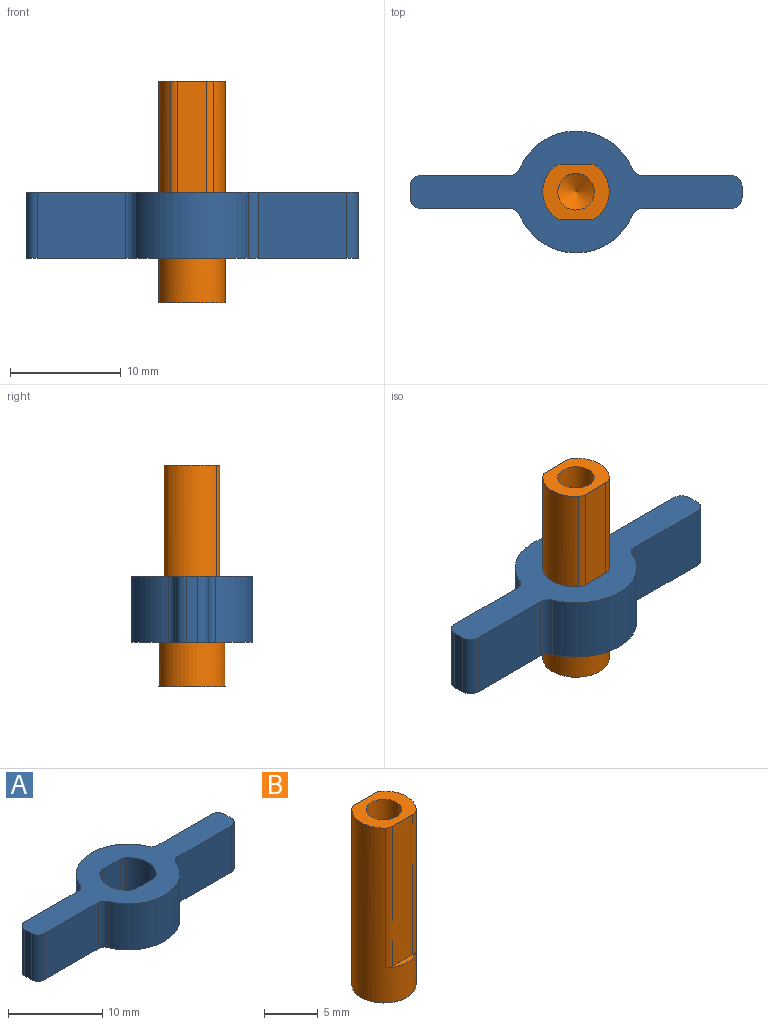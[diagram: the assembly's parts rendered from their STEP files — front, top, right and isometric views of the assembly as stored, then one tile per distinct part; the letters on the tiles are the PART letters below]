
ASSEMBLY  parts=2 mates=1
PART A: 26 faces, bbox 30x11x6 mm
  f0: plane 8x6mm, normal (0,-1,0), area 48mm2, adj f12,f13,f15,f19
  f1: cylinder r=5.5mm len=10.15mm, axis (0,0,-1), area 77.6mm2, adj f12,f13,f19,f20
  f2: plane 8x6mm, normal (0,-1,0), area 48mm2, adj f12,f13,f16,f20
  f3: plane 6x1mm, normal (1,0,0), area 6mm2, adj f12,f13,f16,f17
  f4: plane 8x6mm, normal (0,1,0), area 48mm2, adj f12,f13,f17,f23
  f5: cylinder r=5.5mm len=10.15mm, axis (0,0,-1), area 77.6mm2, adj f12,f13,f22,f23
  f6: plane 8x6mm, normal (0,1,0), area 48mm2, adj f12,f13,f14,f22
  f7: cylinder r=3mm len=6mm, axis (0,0,-1), area 30.5mm2, adj f12,f13,f18,f24
  f8: plane 6x2.65mm, normal (0,-1,0), area 15.9mm2, adj f12,f13,f24,f25
  f9: cylinder r=3mm len=6mm, axis (0,0,-1), area 30.5mm2, adj f12,f13,f21,f25
  f10: plane 6x2.65mm, normal (0,1,0), area 15.9mm2, adj f12,f13,f18,f21
  f11: plane 6x1mm, normal (-1,0,0), area 6mm2, adj f12,f13,f14,f15
  f12: plane 30x11mm, normal (0,0,1), area 126mm2, adj f0,f1,f2,f3,f4,f5,f6,f7
  f13: plane 30x11mm, normal (0,0,-1), area 126mm2, adj f0,f1,f2,f3,f4,f5,f6,f7
  f14: cylinder r=1mm len=6mm, axis (0,0,1), area 9.4mm2, adj f6,f11,f12,f13
  f15: cylinder r=1mm len=6mm, axis (0,0,-1), area 9.4mm2, adj f0,f11,f12,f13
  f16: cylinder r=1mm len=6mm, axis (0,0,1), area 9.4mm2, adj f2,f3,f12,f13
  f17: cylinder r=1mm len=6mm, axis (0,0,-1), area 9.4mm2, adj f3,f4,f12,f13
  f18: cylinder r=1mm len=6mm, axis (0,0,-1), area 4.3mm2, adj f7,f10,f12,f13
  f19: cylinder r=1mm len=6mm, axis (0,0,-1), area 7.1mm2, adj f0,f1,f12,f13
  f20: cylinder r=1mm len=6mm, axis (0,0,-1), area 7.1mm2, adj f1,f2,f12,f13
  f21: cylinder r=1mm len=6mm, axis (0,0,-1), area 4.3mm2, adj f9,f10,f12,f13
  f22: cylinder r=1mm len=6mm, axis (0,0,-1), area 7.1mm2, adj f5,f6,f12,f13
  f23: cylinder r=1mm len=6mm, axis (0,0,-1), area 7.1mm2, adj f4,f5,f12,f13
  f24: cylinder r=1mm len=6mm, axis (0,0,-1), area 4.3mm2, adj f7,f8,f12,f13
  f25: cylinder r=1mm len=6mm, axis (0,0,-1), area 4.3mm2, adj f8,f9,f12,f13
PART B: 13 faces, bbox 6x6x20 mm
  f0: plane 6x5mm, normal (0,0,1), area 17.4mm2, adj f1,f3,f5,f7,f9,f10,f11,f12
  f1: cylinder r=3mm len=20mm, axis (0,0,-1), area 238.2mm2, adj f0,f2,f4,f6,f9,f10,f11,f12
  f2: plane 6x6mm, normal (0,0,-1), area 28.3mm2, adj f1
  f3: plane 16x2.65mm, normal (0,1,0), area 42.3mm2, adj f0,f4,f9,f10
  f4: plane 3.97x0.75mm, normal (0,0,1), area 1.2mm2, adj f1,f3,f9,f10
  f5: plane 16x2.65mm, normal (0,-1,0), area 42.3mm2, adj f0,f6,f11,f12
  f6: plane 3.97x0.75mm, normal (0,0,1), area 1.2mm2, adj f1,f5,f11,f12
  f7: cylinder r=1.65mm len=12mm, axis (0,0,1), area 124.4mm2, adj f0,f8
  f8: cone r=0mm half-angle=59deg, axis (0,0,1), area 10mm2, adj f7
  f9: cylinder r=1mm len=16mm, axis (0,0,-1), area 11.6mm2, adj f0,f1,f3,f4
  f10: cylinder r=1mm len=16mm, axis (0,0,-1), area 11.6mm2, adj f0,f1,f3,f4
  f11: cylinder r=1mm len=16mm, axis (0,0,-1), area 11.6mm2, adj f0,f1,f5,f6
  f12: cylinder r=1mm len=16mm, axis (0,0,-1), area 11.6mm2, adj f0,f1,f5,f6
PLACE A t=(-0.04,-0.03,-16.01)mm
PLACE B t=(-0.04,-0.03,-20.01)mm fixed
MATE slider A.f1 <-> B.f1  axis (0,0,1) through (-0.04,-0.03,-10.01)mm
